# Revit family: IRB 500 A3 EC_7890040
name_source: partatom
category: Mechanical Equipment
revit_build: Autodesk Revit MEP 2014 (Build: 20130308_1515(x64)
units: mm (PartAtom-declared; Revit-internal decimal feet)

## types (1)
- IRB 500 A3 EC
    Capacitor = - µF
    Current = 2 A
    Depth = 681 mm  [stored 2.23425 ft]
    Description = Insulated duct fans with circular connections
    Diameter = 500 mm  [stored 1.64042 ft]
    Frequency = 50 Hz
    Height = 908 mm  [stored 2.979 ft]
    Main Material = Steel, Galvanized
    Max. temperature of transported air = 60 °C
    Max. temperature of transported air when speed controlled = 60 °C
    Phase = 3
    Power = 981 W
    Sound pressure level at 3 m = 59 dB(A)
    Speed = 1340 rpm
    Voltage = 400 V
    Voltage range = 380-480 V
    Weight = 79.70 kg
    Width = 1110 mm  [stored 3.64173 ft]
    Wiring diagram = 4040147

note: [stored X ft] marks values corroborated as IEEE doubles in the binary element streams (Revit-internal decimal feet)

## geometry (parser evidence)
native form markers: Sweep x3
no freeform markers — native parametric forms only
